# Revit family: Electronics_Switches_Biamp_NMS-NG10GPX-AVB_GSM4212PX
name_source: partatom
category: Communication Devices
units: mm (PartAtom-declared; Revit-internal decimal feet)

## family parameters
Cut with Voids When Loaded = No
Host = Face
Maintain Annotation Orientation = No
OmniClass Number = 23.80.50.11.14
OmniClass Title = Switches
Part Type = Normal
Room Calculation Point = No
Round Connector Dimension = Use Diameter
Shared = No

## types (1)
- NMS-NG10GPX-AVB
    AVB Support = Yes. Electronic license required, activation key sent via email (AVB4212PX-10000S)
    Acoustics = Fanless or 39.22dB@25ºC
    Apparent Load = 306 VA
    Connector Description = Power connector, 120V
    Current = 5 A
    Default Elevation = 1219 mm
    Depth = 200 mm  [stored 0.656168 ft]
    Description = The NMS-NG10GPX-AVB (NETGEAR model GSM4212PX) switch is designed to seamlessly integrate with Cambridge QT X sound masking solutions for optimal network performance.
    Height = 43 mm
    Housing Material = Biamp - Plastic - Black
    IGMP Support = Enhanced (NETGEAR IGMP Plus™)
    Jumbo Frame Support = Yes, up to 12kb
    Manufacturer = Biamp
    Max Power Consumption = 306 W
    Model = NMS-NG10GPX-AVB
    Nom Longer bracket = Longer bracket
    Nom Standard bracket = Standard bracket
    Nom Surface = Surface
    Number of Poles = 1
    Number of Ports = 12 (10x 1G, 2x SFP+)
    PoE Ports / Budget = 8 PoE+ (30W/port), 240W Budget
    Power Factor = 1
    Primary Port Speed = 1 Gigabit
    Product Documentation Link = https://downloads.biamp.com
    Product Page URL = https://www.biamp.com
    Product data url = https://bimobject.com
    Third party support = Domotz
    URL = https://www.biamp.com
    Version = 1
    Voltage = 120 V
    Weight = 6.39 lb
    Width = 440 mm  [stored 1.44357 ft]

note: [stored X ft] marks values corroborated as IEEE doubles in the binary element streams (Revit-internal decimal feet)

## geometry (parser evidence)
native form markers: Sweep x13
no freeform markers — native parametric forms only
